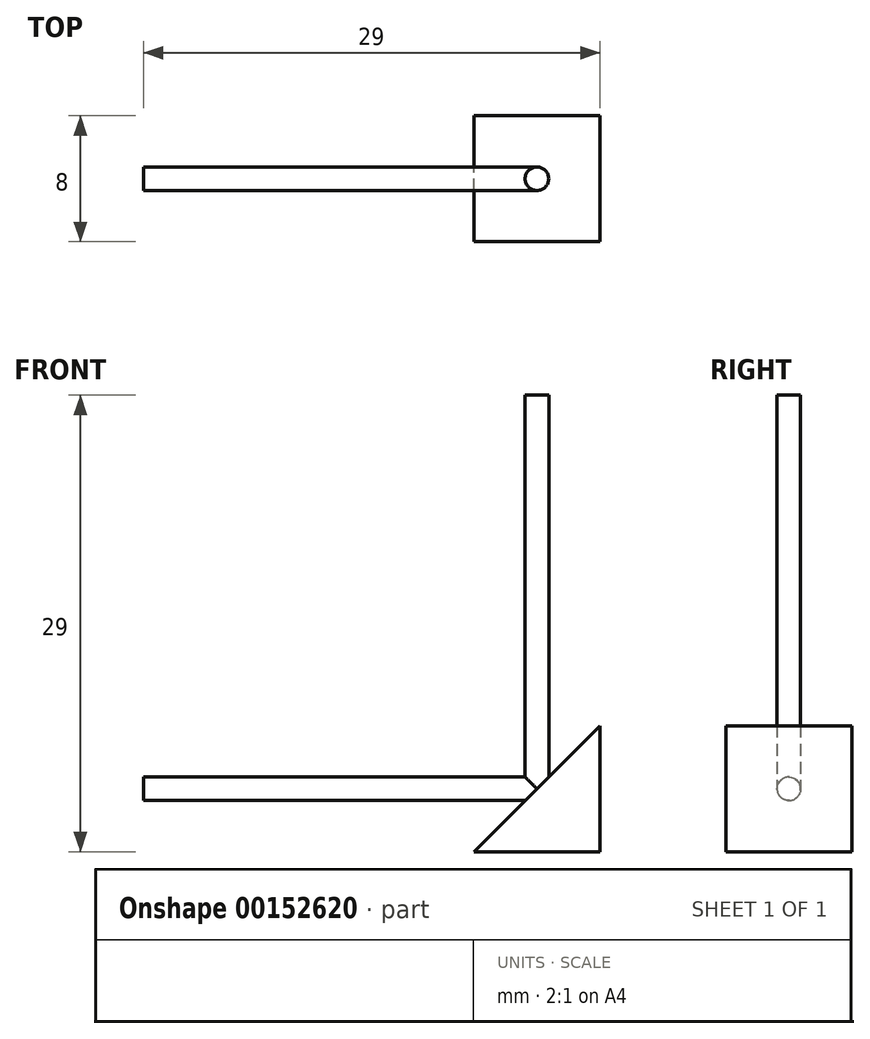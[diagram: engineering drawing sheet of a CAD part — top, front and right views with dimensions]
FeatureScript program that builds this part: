
annotation { "Feature Type Name" : "Feature", "Feature Type Description" : "" }
export const myFeature = defineFeature(function(context is Context, id is Id, definition is map)
    precondition{}
    {
        {
            var Q0;
            Q0=qCreatedBy(makeId("Front.planeOp"),FACE);
            var sketch = newSketch(context, id + "F0", { "sketchPlane" : qUnion([Q0])});
            skLineSegment(sketch, "E0.bottom", {"start": v(-4, 4) * mm, "end": v(4, 4) * mm});
            skLineSegment(sketch, "E0.top", {"start": v(-4, -4) * mm, "end": v(4, -4) * mm});
            skLineSegment(sketch, "E0.left", {"start": v(-4, 4) * mm, "end": v(-4, -4) * mm});
            skLineSegment(sketch, "E0.right", {"start": v(4, 4) * mm, "end": v(4, -4) * mm});
            skPoint(sketch, "E0.middle", {"position": v(0, 0) * mm});
            skLineSegment(sketch, "E1", {"start": v(-4, -4) * mm, "end": v(4, 4) * mm});
            skSolve(sketch);
        }
        {
            var Q0;
            Q0=makeQuery(id+"F0.imprint","IMPRINT",FACE,{"disambiguationData":[TD([[makeQuery(id+"F0.imprint","IMPRINT",EDGE,{"derivedFrom":sQuery(id+"F0.wireOp",EDGE,"E0.top")}),1.0]])]});
            extrude(context, id + "F1", {"entities" : qUnion([Q0]), "endBound" : BoundingType.SYMMETRIC, "depth" : 8 * mm});
        }
        {
            var Q0;
            Q0=qCreatedBy(makeId("Top.planeOp"),FACE);
            var sketch = newSketch(context, id + "F2", { "sketchPlane" : qUnion([Q0])});
            skCircle(sketch, "E2", {"center": v(0, 0) * mm, "radius": 0.75 * mm});
            skSolve(sketch);
        }
        {
            var Q0;
            Q0=makeQuery(id+"F2.imprint","IMPRINT",FACE,{"disambiguationData":[TD([[makeQuery(id+"F2.imprint","IMPRINT",EDGE,{"derivedFrom":sQuery(id+"F2.wireOp",EDGE,"E2")}),1.0]])]});
            extrude(context, id + "F3", {"entities" : qUnion([Q0]), "operationType" : NewBodyOperationType.ADD, "depth" : 25 * mm});
        }
        {
            var Q0;
            Q0=qCreatedBy(makeId("Right.planeOp"),FACE);
            var sketch = newSketch(context, id + "F4", { "sketchPlane" : qUnion([Q0])});
            skCircle(sketch, "E3", {"center": v(0, 0) * mm, "radius": 0.75 * mm});
            skSolve(sketch);
        }
        {
            var Q0;
            Q0 = qSketchRegion(id + "F4", true);
            extrude(context, id + "F5", {"entities" : qUnion([Q0]), "operationType" : NewBodyOperationType.ADD, "oppositeDirection" : true, "depth" : 25 * mm});
        }
    });
